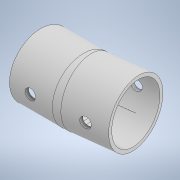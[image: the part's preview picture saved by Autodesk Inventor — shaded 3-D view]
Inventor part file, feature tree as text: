
AUTODESK INVENTOR PART (.ipt)
format: ipt  version: 2022 (Build 260153000, 153)  size: 242,176 bytes
history: native  units: mm
features: sketch x4, extrude x2, sweep x1
ambient origin geometry x8: Origin, YZ Plane, XZ Plane, XY Plane, X Axis, Y Axis, Z Axis, Center Point
bodies: Body1 (feature_tree)
feature tree (7):
  sweep  "Sweep1"
  extrude  "Extrusion8"  Depth=30.194196mm
  extrude  "Extrusion9"  Depth=10.0mm
  sketch  "Sketch5"  dims[d31=34.456mm d122=13.0mm]
  sketch  "Sketch6"  dims[d123=13.0mm d124=30.194196mm]
  sketch  "Sketch7"  dims[d125=10.0mm d126=16.0mm]
  sketch  "Sketch8"  dims[d127=18.0mm d128=0.0mm d129=0.0mm d130=6.0mm d131=3.0mm d132=25.0mm d133=0.0mm d134=6.0mm d135=3.0mm d136=25.0mm d137=0.0mm d138=0.01mm d139=0.01mm]
